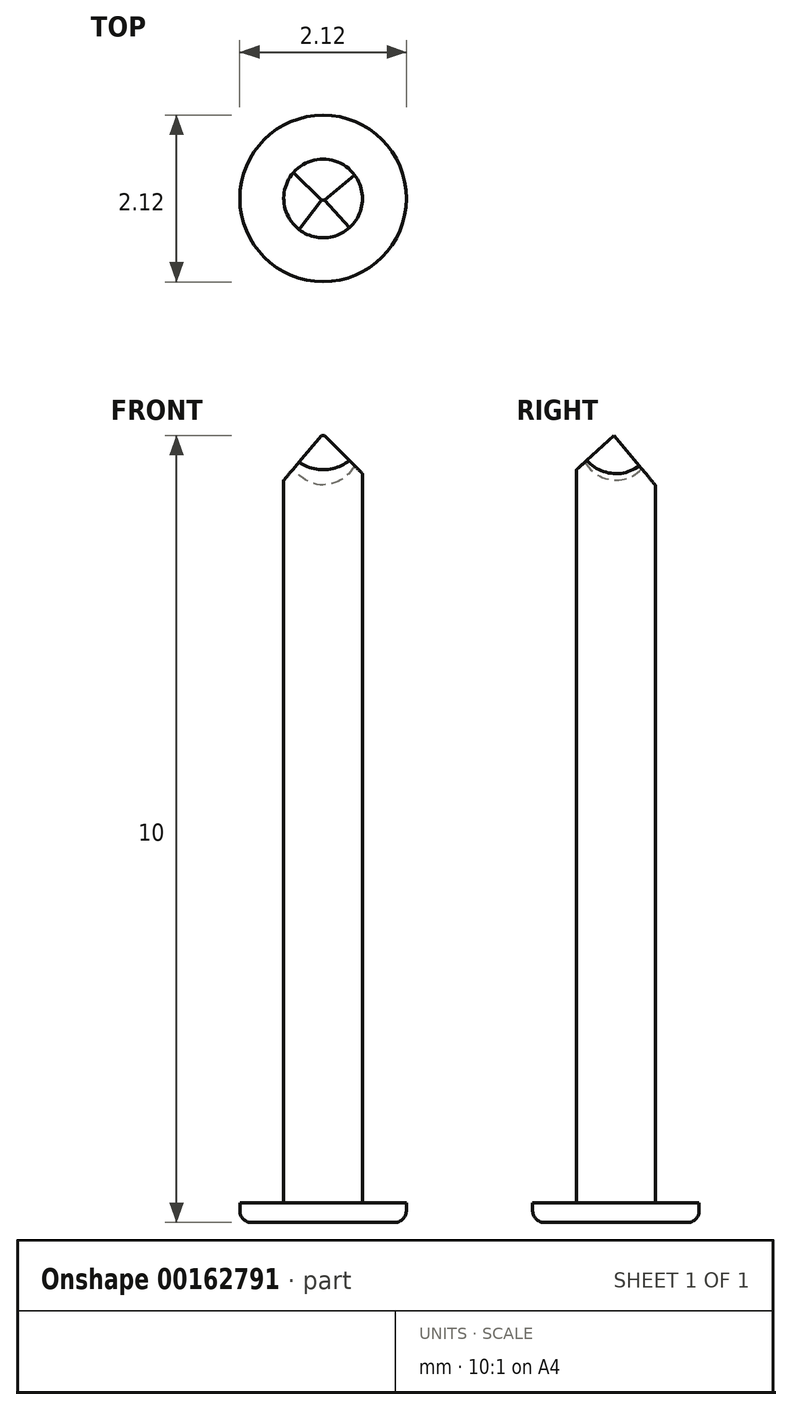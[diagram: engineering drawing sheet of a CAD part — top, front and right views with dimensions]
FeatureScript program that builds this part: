
annotation { "Feature Type Name" : "Feature", "Feature Type Description" : "" }
export const myFeature = defineFeature(function(context is Context, id is Id, definition is map)
    precondition{}
    {
        {
            var Q0;
            Q0=qCreatedBy(makeId("Top.planeOp"),FACE);
            var sketch = newSketch(context, id + "F0", { "sketchPlane" : qUnion([Q0])});
            skCircle(sketch, "E0", {"center": v(0, 0) * mm, "radius": 0.5 * mm});
            skCircle(sketch, "E1", {"center": v(0, 0) * mm, "radius": 1.06 * mm});
            skSolve(sketch);
        }
        {
            var Q0;
            Q0=makeQuery(id+"F0.imprint","IMPRINT",FACE,{"disambiguationData":[TD([[makeQuery(id+"F0.imprint","IMPRINT",EDGE,{"derivedFrom":sQuery(id+"F0.wireOp",EDGE,"E0")}),1.0]])]});
            extrude(context, id + "F1", {"entities" : qUnion([Q0]), "depth" : 10 * mm});
        }
        {
            var Q0;
            Q0=makeQuery(id+"F0.imprint","IMPRINT",FACE,{"disambiguationData":[TD([[makeQuery(id+"F0.imprint","IMPRINT",EDGE,{"derivedFrom":sQuery(id+"F0.wireOp",EDGE,"E0")}),-1.0]])]});
            extrude(context, id + "F2", {"entities" : qUnion([Q0]), "operationType" : NewBodyOperationType.ADD, "depth" : .25 * mm});
        }
        {
            var Q0;
            Q0=makeQuery(id+"F2.opExtrude","CAP_EDGE",EDGE,{"disambiguationData":[OSD([sQuery(id+"F0.wireOp",EDGE,"E1")])],"isStart":true});
            fillet(context, id + "F3", {"entities" : qUnion([Q0]), "radius" : .15 * mm, "tangentPropagation" : true, "allowEdgeOverflow" : false});
        }
        {
            var Q0;
            Q0=qCreatedBy(makeId("Right.planeOp"),FACE);
            var sketch = newSketch(context, id + "F4", { "sketchPlane" : qUnion([Q0])});
            skLineSegment(sketch, "E2", {"start": v(-0.02, 10) * mm, "end": v(0.7, 9.14) * mm});
            skLineSegment(sketch, "E3", {"start": v(0.7, 9.14) * mm, "end": v(0.7, 10.35) * mm});
            skLineSegment(sketch, "E4", {"start": v(0.7, 10.35) * mm, "end": v(-0.87, 10.4) * mm});
            skLineSegment(sketch, "E5", {"start": v(-0.87, 10.4) * mm, "end": v(-0.96, 9.15) * mm});
            skLineSegment(sketch, "E6", {"start": v(-0.96, 9.15) * mm, "end": v(-0.02, 10) * mm});
            skSolve(sketch);
        }
        {
            var Q0;
            Q0 = qSketchRegion(id + "F4", true);
            extrude(context, id + "F5", {"entities" : qUnion([Q0]), "operationType" : NewBodyOperationType.REMOVE, "depth" : 25 * mm, "hasSecondDirection" : true, "secondDirectionOppositeDirection" : true, "secondDirectionDepth" : 25 * mm});
        }
        {
            var Q0;
            Q0=qCreatedBy(makeId("Front.planeOp"),FACE);
            var sketch = newSketch(context, id + "F6", { "sketchPlane" : qUnion([Q0])});
            skLineSegment(sketch, "E7", {"start": v(0, 10.02) * mm, "end": v(-1.29, 8.5) * mm});
            skLineSegment(sketch, "E8", {"start": v(-1.29, 8.5) * mm, "end": v(-1.29, 10.74) * mm});
            skLineSegment(sketch, "E9", {"start": v(-1.29, 10.74) * mm, "end": v(1.13, 10.74) * mm});
            skLineSegment(sketch, "E10", {"start": v(1.13, 10.74) * mm, "end": v(1.33, 8.67) * mm});
            skLineSegment(sketch, "E11", {"start": v(1.33, 8.67) * mm, "end": v(0, 10.02) * mm});
            skSolve(sketch);
        }
        {
            var Q0;
            Q0=makeQuery(id+"F6.imprint","IMPRINT",FACE,{"disambiguationData":[TD([[makeQuery(id+"F6.imprint","IMPRINT",EDGE,{"derivedFrom":sQuery(id+"F6.wireOp",EDGE,"E7")}),-1.0]])]});
            extrude(context, id + "F7", {"entities" : qUnion([Q0]), "operationType" : NewBodyOperationType.REMOVE, "depth" : 25 * mm, "hasSecondDirection" : true, "secondDirectionOppositeDirection" : true, "secondDirectionDepth" : 25 * mm});
        }
    });
